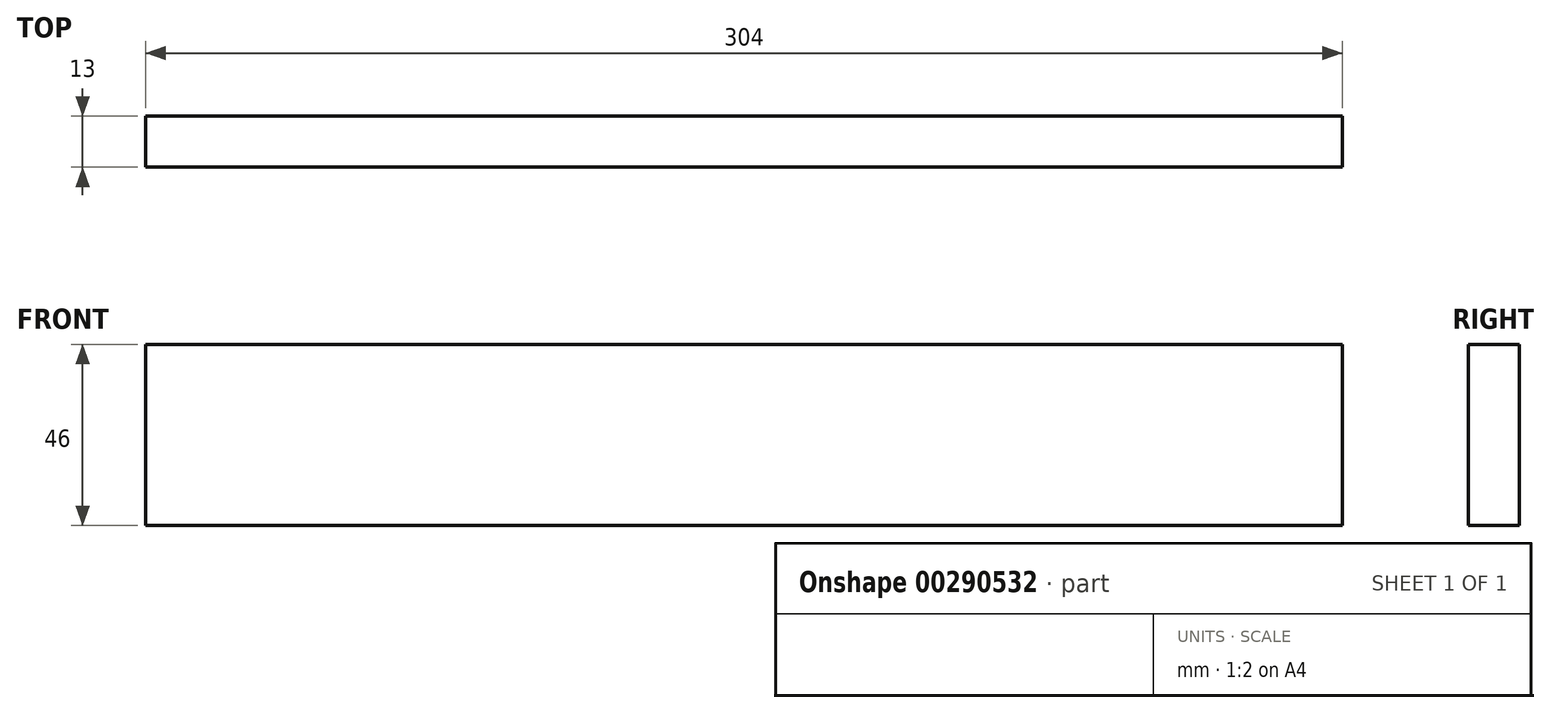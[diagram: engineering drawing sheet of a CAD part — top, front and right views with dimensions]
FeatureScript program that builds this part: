
annotation { "Feature Type Name" : "Feature", "Feature Type Description" : "" }
export const myFeature = defineFeature(function(context is Context, id is Id, definition is map)
    precondition{}
    {
        {
            var Q0;
            Q0=qCreatedBy(makeId("Front.planeOp"),FACE);
            var sketch = newSketch(context, id + "F0", { "sketchPlane" : qUnion([Q0])});
            skLineSegment(sketch, "E0.bottom", {"start": v(152, -23) * mm, "end": v(-152, -23) * mm});
            skLineSegment(sketch, "E0.top", {"start": v(152, 23) * mm, "end": v(-152, 23) * mm});
            skLineSegment(sketch, "E0.left", {"start": v(152, -23) * mm, "end": v(152, 23) * mm});
            skLineSegment(sketch, "E0.right", {"start": v(-152, -23) * mm, "end": v(-152, 23) * mm});
            skPoint(sketch, "E0.middle", {"position": v(0, 0) * mm});
            skSolve(sketch);
        }
        {
            var Q0;
            Q0 = qSketchRegion(id + "F0", true);
            extrude(context, id + "F1", {"entities" : qUnion([Q0]), "depth" : 13 * mm});
        }
    });
